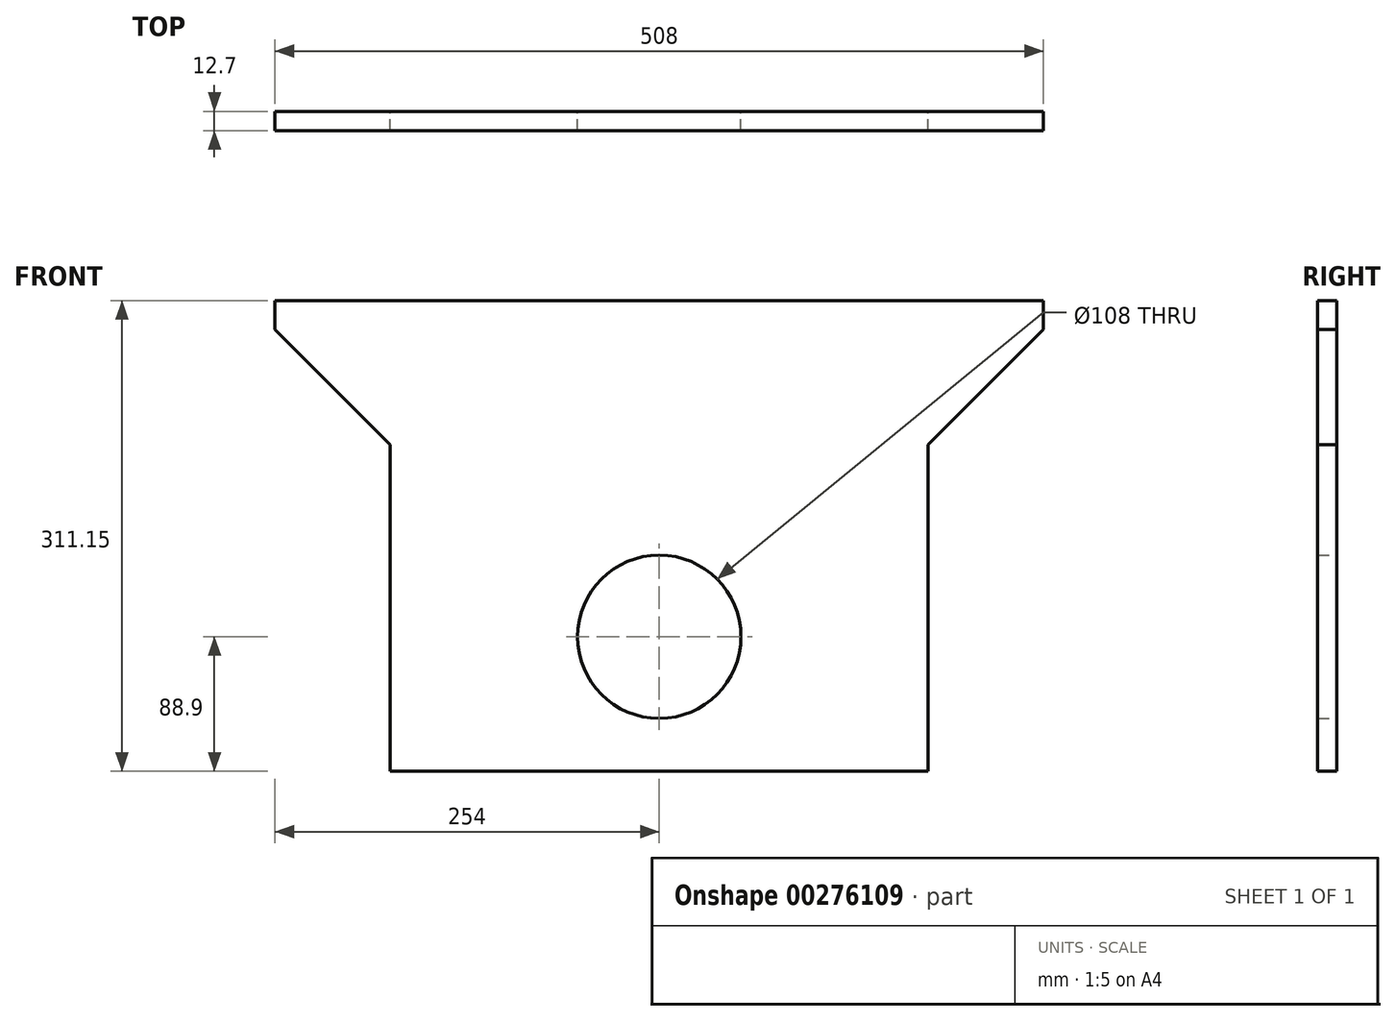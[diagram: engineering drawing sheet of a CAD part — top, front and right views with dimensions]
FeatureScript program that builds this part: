
annotation { "Feature Type Name" : "Feature", "Feature Type Description" : "" }
export const myFeature = defineFeature(function(context is Context, id is Id, definition is map)
    precondition{}
    {
        {
            var Q0;
            Q0=qCreatedBy(makeId("Front.planeOp"),FACE);
            var sketch = newSketch(context, id + "F0", { "sketchPlane" : qUnion([Q0])});
            skLineSegment(sketch, "E0", {"start": v(254, 0) * mm, "end": v(50.8, -203.2) * mm});
            skLineSegment(sketch, "E1", {"start": v(-254, 0) * mm, "end": v(-50.8, -203.2) * mm});
            skLineSegment(sketch, "E2", {"start": v(0, -203.2) * mm, "end": v(-187.32, -203.2) * mm, "construction": true});
            skLineSegment(sketch, "E3", {"start": v(0, -203.2) * mm, "end": v(193.28, -203.2) * mm, "construction": true});
            skLineSegment(sketch, "E4", {"start": v(-254, 0) * mm, "end": v(254, 0) * mm, "construction": true});
            skLineSegment(sketch, "E5", {"start": v(-254, 0) * mm, "end": v(-254, 19.05) * mm});
            skLineSegment(sketch, "E6", {"start": v(-254, 19.05) * mm, "end": v(254, 19.05) * mm});
            skLineSegment(sketch, "E7", {"start": v(254, 19.05) * mm, "end": v(254, 0) * mm});
            skLineSegment(sketch, "E8.top", {"start": v(177.8, -292.1) * mm, "end": v(-177.8, -292.1) * mm});
            skLineSegment(sketch, "E8.left", {"start": v(177.8, -76.2) * mm, "end": v(177.8, -292.1) * mm});
            skLineSegment(sketch, "E8.right", {"start": v(-177.8, -76.2) * mm, "end": v(-177.8, -292.1) * mm});
            skPoint(sketch, "E8.middle", {"position": v(0, -203.2) * mm});
            skPoint(sketch, "E8.bottom.start.orphan", {"position": v(177.8, -114.3) * mm});
            skPoint(sketch, "E9.orphan", {"position": v(-177.8, -114.3) * mm});
            skCircle(sketch, "E10", {"center": v(0, -203.2) * mm, "radius": 54 * mm});
            skSolve(sketch);
        }
        {
            var Q0;
            {var subQ0=sQuery(id+"F0.wireOp",EDGE,"E5");Q0=makeQuery(id+"F0.imprint","IMPRINT",FACE,{"disambiguationData":[TD([[makeQuery(id+"F0.imprint","IMPRINT",EDGE,{"derivedFrom":subQ0}),-1.0]])]});}
            var Q1;
            Q1=makeQuery(id+"F0.imprint","IMPRINT",FACE,{"disambiguationData":[TD([[makeQuery(id+"F0.imprint","IMPRINT",EDGE,{"derivedFrom":sQuery(id+"F0.wireOp",EDGE,"E8.top")}),-1.0]])]});
            extrude(context, id + "F1", {"entities" : qUnion([Q0, Q1]), "depth" : 12.7 * mm});
        }
    });
